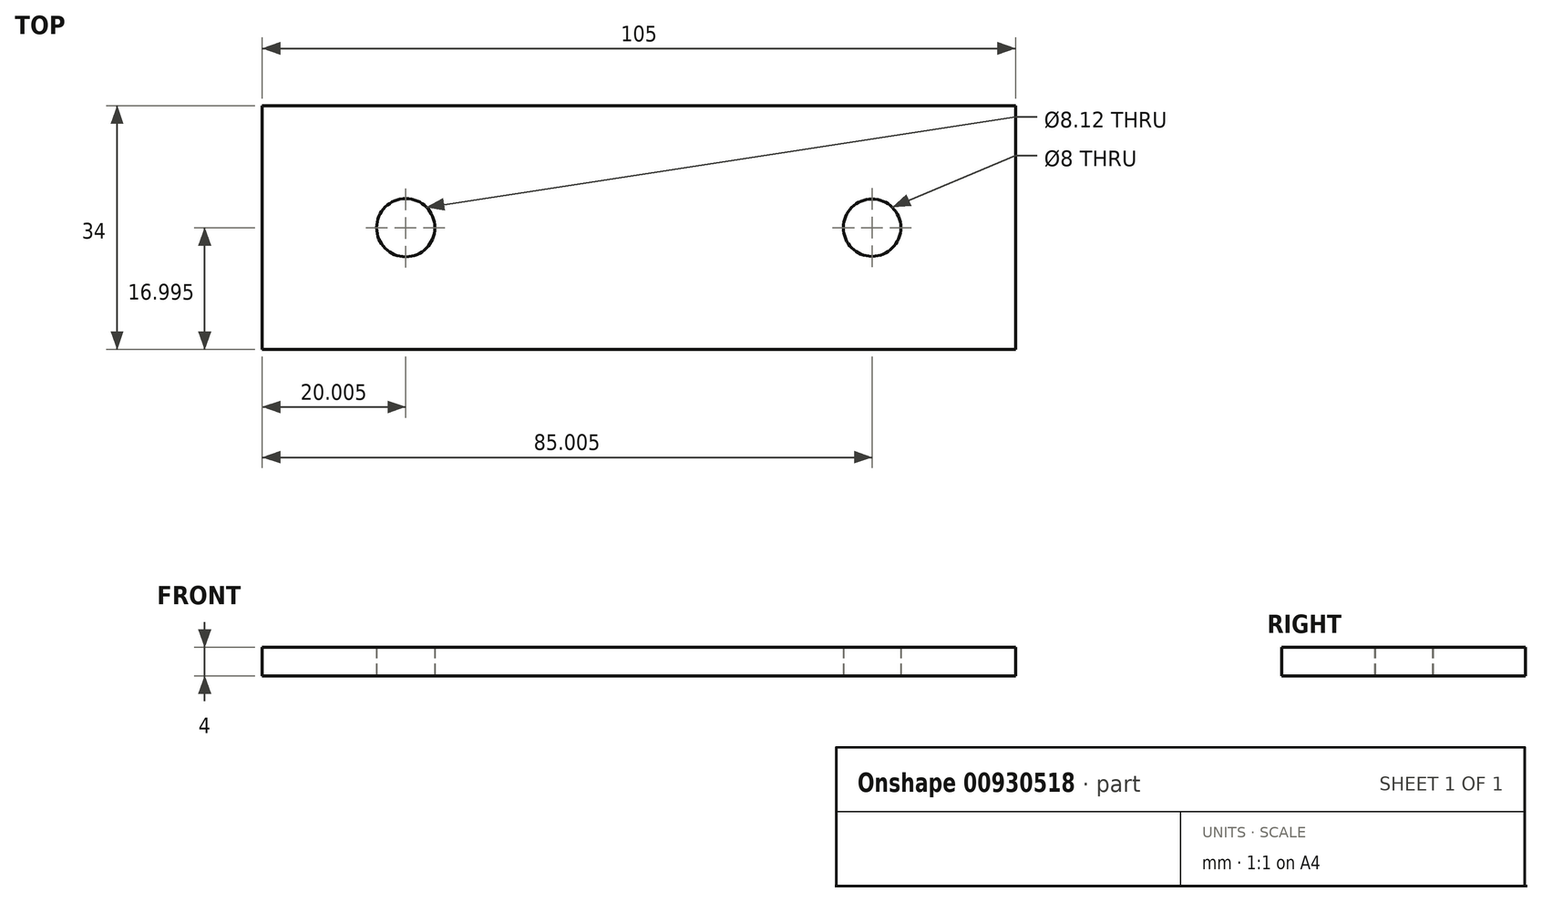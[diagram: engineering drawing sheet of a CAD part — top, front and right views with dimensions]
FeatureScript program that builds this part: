
annotation { "Feature Type Name" : "Feature", "Feature Type Description" : "" }
export const myFeature = defineFeature(function(context is Context, id is Id, definition is map)
    precondition{}
    {
        {
            var Q0;
            Q0=qCreatedBy(makeId("Top.planeOp"),FACE);
            var sketch = newSketch(context, id + "F0", { "sketchPlane" : qUnion([Q0])});
            skLineSegment(sketch, "E0.bottom", {"start": v(-30.64, 8.65) * mm, "end": v(74.36, 8.65) * mm});
            skLineSegment(sketch, "E0.top", {"start": v(-30.64, -25.35) * mm, "end": v(74.36, -25.35) * mm});
            skLineSegment(sketch, "E0.left", {"start": v(-30.64, 8.65) * mm, "end": v(-30.64, -25.35) * mm});
            skLineSegment(sketch, "E0.right", {"start": v(74.36, 8.65) * mm, "end": v(74.36, -25.35) * mm});
            skCircle(sketch, "E1", {"center": v(-10.64, -8.35) * mm, "radius": 4.06 * mm});
            skCircle(sketch, "E2", {"center": v(54.36, -8.35) * mm, "radius": 4 * mm});
            skSolve(sketch);
        }
        {
            var Q0;
            Q0 = qSketchRegion(id + "F0", true);
            extrude(context, id + "F1", {"entities" : qUnion([Q0]), "depth" : 4 * mm, "offsetDistance" : 25 * mm});
        }
    });
